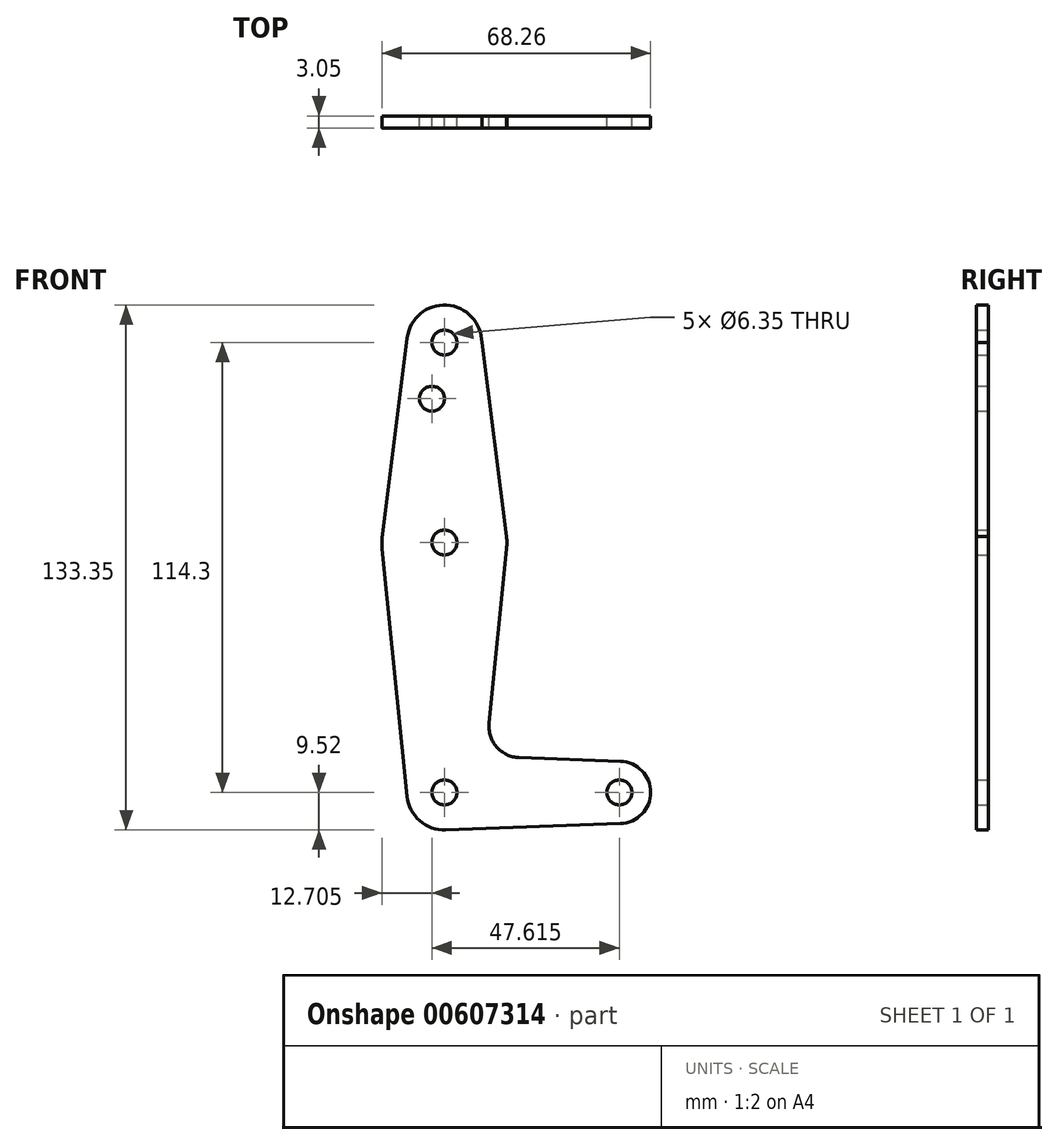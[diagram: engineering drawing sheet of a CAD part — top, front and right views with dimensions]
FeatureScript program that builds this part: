
annotation { "Feature Type Name" : "Feature", "Feature Type Description" : "" }
export const myFeature = defineFeature(function(context is Context, id is Id, definition is map)
    precondition{}
    {
        {
            var Q0;
            Q0=qCreatedBy(makeId("Front.planeOp"),FACE);
            var sketch = newSketch(context, id + "F0", { "sketchPlane" : qUnion([Q0])});
            skLineSegment(sketch, "E0", {"start": v(0, 0) * mm, "end": v(44.45, 0) * mm});
            skLineSegment(sketch, "E1", {"start": v(0, 0) * mm, "end": v(0, 63.5) * mm});
            skCircle(sketch, "E2", {"center": v(0, 0) * mm, "radius": 9.53 * mm});
            skCircle(sketch, "E3", {"center": v(0, 63.5) * mm, "radius": 15.88 * mm});
            skLineSegment(sketch, "E4", {"start": v(0, 63.5) * mm, "end": v(0, 114.3) * mm});
            skCircle(sketch, "E5", {"center": v(0, 114.3) * mm, "radius": 9.53 * mm});
            skCircle(sketch, "E6", {"center": v(44.45, 0) * mm, "radius": 7.94 * mm});
            skLineSegment(sketch, "E7", {"start": v(18.97, 8.85) * mm, "end": v(44.73, 7.93) * mm});
            skLineSegment(sketch, "E8", {"start": v(0.34, -9.52) * mm, "end": v(44.73, -7.93) * mm});
            skLineSegment(sketch, "E9", {"start": v(-9.48, -0.95) * mm, "end": v(-15.8, 61.91) * mm});
            skLineSegment(sketch, "E10", {"start": v(15.8, 61.91) * mm, "end": v(11.34, 17.6) * mm});
            skLineSegment(sketch, "E11", {"start": v(-9.45, 115.5) * mm, "end": v(-15.75, 65.48) * mm});
            skLineSegment(sketch, "E12", {"start": v(9.53, 114.3) * mm, "end": v(15.8, 65.09) * mm});
            skCircle(sketch, "E13", {"center": v(0, 114.3) * mm, "radius": 3.18 * mm});
            skCircle(sketch, "E14", {"center": v(0, 63.5) * mm, "radius": 3.18 * mm});
            skCircle(sketch, "E15", {"center": v(0, 0) * mm, "radius": 3.18 * mm});
            skCircle(sketch, "E16", {"center": v(44.45, 0) * mm, "radius": 3.18 * mm});
            skCircle(sketch, "E17", {"center": v(-3.17, 100.03) * mm, "radius": 3.18 * mm});
            skArc(sketch, "E18.filletArc", {"start": v(11.34, 17.6) * mm, "mid": v(13.26, 11.57) * mm, "end": v(18.97, 8.85) * mm});
            skSolve(sketch);
        }
        {
            var Q0;
            {var subQ5=sQuery(id+"F0.wireOp",EDGE,"E7");Q0=makeQuery(id+"F0.imprint","IMPRINT",FACE,{"disambiguationData":[TD([[makeQuery(id+"F0.imprint","IMPRINT",EDGE,{"derivedFrom":subQ5}),-1.0]])]});}
            var Q1;
            {var subQ5=sQuery(id+"F0.wireOp",EDGE,"E9");Q1=makeQuery(id+"F0.imprint","IMPRINT",FACE,{"disambiguationData":[TD([[makeQuery(id+"F0.imprint","IMPRINT",EDGE,{"derivedFrom":subQ5}),-1.0]])]});}
            var Q2;
            {var subQ0=sQuery(id+"F0.wireOp",EDGE,"E3");var subQ5=sQuery(id+"F0.wireOp",EDGE,"E1");var subQ6=makeQuery(id+"F0.imprint","INTERSECT",VERTEX,{"derivedFrom":[subQ5,subQ0]});Q2=makeQuery(id+"F0.imprint","IMPRINT",FACE,{"disambiguationData":[TD([[makeQuery(id+"F0.imprint","IMPRINT",EDGE,{"disambiguationData":[TD([[subQ6,-1.0]])],"derivedFrom":subQ5}),1.0]])]});}
            var Q3;
            {var subQ0=sQuery(id+"F0.wireOp",EDGE,"E3");var subQ2=sQuery(id+"F0.wireOp",EDGE,"E1");var subQ3=makeQuery(id+"F0.imprint","INTERSECT",VERTEX,{"derivedFrom":[subQ2,subQ0]});Q3=makeQuery(id+"F0.imprint","IMPRINT",FACE,{"disambiguationData":[TD([[makeQuery(id+"F0.imprint","IMPRINT",EDGE,{"disambiguationData":[TD([[subQ3,-1.0]])],"derivedFrom":subQ2}),-1.0]])]});}
            var Q4;
            {var subQ0=sQuery(id+"F0.wireOp",EDGE,"E11");Q4=makeQuery(id+"F0.imprint","IMPRINT",FACE,{"disambiguationData":[TD([[makeQuery(id+"F0.imprint","IMPRINT",EDGE,{"derivedFrom":subQ0}),1.0]])]});}
            var Q5;
            {var subQ0=sQuery(id+"F0.wireOp",EDGE,"E12");var subQ5=sQuery(id+"F0.wireOp",EDGE,"E3");var subQ10=makeQuery(id+"F0.imprint","INTERSECT",VERTEX,{"disambiguationData":[OD(1.0)],"derivedFrom":[subQ5,subQ0]});Q5=makeQuery(id+"F0.imprint","IMPRINT",FACE,{"disambiguationData":[TD([[makeQuery(id+"F0.imprint","IMPRINT",EDGE,{"disambiguationData":[TD([[subQ10,-1.0]])],"derivedFrom":subQ5}),-1.0]])]});}
            var Q6;
            Q6=makeQuery(id+"F0.imprint","IMPRINT",FACE,{"disambiguationData":[TD([[makeQuery(id+"F0.imprint","IMPRINT",EDGE,{"derivedFrom":sQuery(id+"F0.wireOp",EDGE,"E13")}),-1.0]])]});
            var Q7;
            {var subQ5=sQuery(id+"F0.wireOp",EDGE,"E8");Q7=makeQuery(id+"F0.imprint","IMPRINT",FACE,{"disambiguationData":[TD([[makeQuery(id+"F0.imprint","IMPRINT",EDGE,{"derivedFrom":subQ5}),1.0]])]});}
            var Q8;
            {var subQ5=sQuery(id+"F0.wireOp",EDGE,"E15");var subQ7=sQuery(id+"F0.wireOp",EDGE,"E0");var subQ8=makeQuery(id+"F0.imprint","INTERSECT",VERTEX,{"derivedFrom":[subQ7,subQ5]});Q8=makeQuery(id+"F0.imprint","IMPRINT",FACE,{"disambiguationData":[TD([[makeQuery(id+"F0.imprint","IMPRINT",EDGE,{"disambiguationData":[TD([[subQ8,-1.0]])],"derivedFrom":subQ7}),-1.0]])]});}
            var Q9;
            Q9=makeQuery(id+"F0.imprint","IMPRINT",FACE,{"disambiguationData":[TD([[makeQuery(id+"F0.imprint","IMPRINT",EDGE,{"derivedFrom":sQuery(id+"F0.wireOp",EDGE,"E16")}),-1.0]])]});
            var Q10;
            {var subQ0=sQuery(id+"F0.wireOp",EDGE,"E15");var subQ1=sQuery(id+"F0.wireOp",EDGE,"E0");var subQ2=makeQuery(id+"F0.imprint","INTERSECT",VERTEX,{"derivedFrom":[subQ1,subQ0]});Q10=makeQuery(id+"F0.imprint","IMPRINT",FACE,{"disambiguationData":[TD([[makeQuery(id+"F0.imprint","IMPRINT",EDGE,{"disambiguationData":[TD([[subQ2,-1.0]])],"derivedFrom":subQ1}),1.0]])]});}
            extrude(context, id + "F1", {"entities" : qUnion([Q0, Q1, Q2, Q3, Q4, Q5, Q6, Q7, Q8, Q9, Q10]), "depth" : 3.05 * mm, "offsetDistance" : 25.4 * mm});
        }
    });
